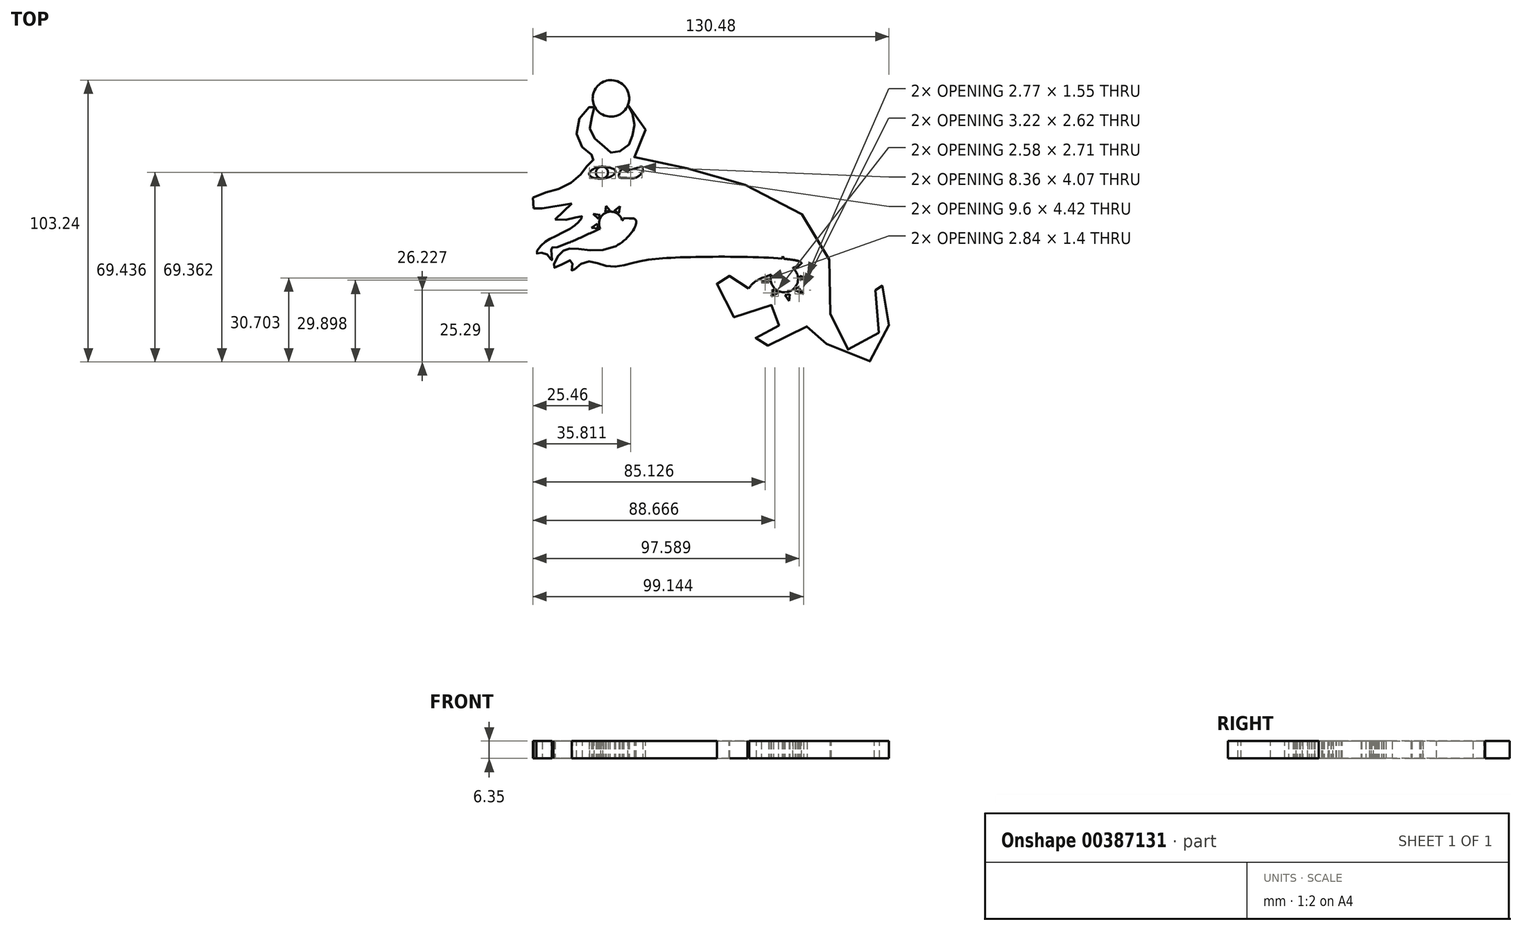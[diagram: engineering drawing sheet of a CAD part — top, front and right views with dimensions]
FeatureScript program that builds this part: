
annotation { "Feature Type Name" : "Feature", "Feature Type Description" : "" }
export const myFeature = defineFeature(function(context is Context, id is Id, definition is map)
    precondition{}
    {
        {
            var Q0;
            Q0=qCreatedBy(makeId("Top.planeOp"),FACE);
            var sketch = newSketch(context, id + "F0", { "sketchPlane" : qUnion([Q0])});
            skLineSegment(sketch, "E0", {"start": v(-40.42, 42.33) * mm, "end": v(-46.54, 36.47) * mm});
            skPoint(sketch, "E1.86.internal.snap0", {"position": v(-47.78, 39.42) * mm});
            skPoint(sketch, "E1.87.internal.snap0", {"position": v(-47.78, 39.42) * mm});
            skPoint(sketch, "E1.88.internal.snap0", {"position": v(-47.78, 39.42) * mm});
            skPoint(sketch, "E1.92.internal.snap0", {"position": v(-47.78, 39.42) * mm});
            skFitSpline(sketch, "E1", {"points": [v(-54.68, 44.52) * mm, v(-45.52, 47.57) * mm, v(-37.48, 52.65) * mm, v(-34.24, 56.77) * mm, v(-32.19, 59.13) * mm, v(-36, 62.36) * mm, v(-38.07, 72.66) * mm, v(-32.48, 78.25) * mm, v(-32.77, 75) * mm, v(-33.49, 68.4) * mm, v(-28.36, 62.95) * mm, v(-25.42, 60.89) * mm, v(-20.12, 63.24) * mm, v(-18.07, 67.95) * mm, v(-17.77, 74.42) * mm, v(-19.83, 78.54) * mm, v(-15.12, 75.6) * mm, v(-13.36, 71.19) * mm, v(-13.95, 66.18) * mm, v(-15.71, 61.48) * mm, v(-17.48, 59.42) * mm, v(-11, 57.07) * mm, v(8.7, 54.12) * mm, v(24, 48.83) * mm, v(41.65, 40) * mm, v(50.77, 30.89) * mm, v(54.6, 16.18) * mm, v(54.3, 2.94) * mm, v(54.88, -3.24) * mm, v(60.18, -10.88) * mm, v(69, -10.59) * mm, v(71.95, -5.3) * mm, v(72.24, 0) * mm, v(70.77, 10.88) * mm, v(70.77, 17.65) * mm, v(72.83, 13.53) * mm, v(74.6, 8.24) * mm, v(75.77, 0) * mm, v(74.3, -10) * mm, v(69.3, -15.3) * mm, v(61.65, -14.41) * mm, v(51.35, -6.77) * mm, v(49.3, 0) * mm, v(44.3, -4.12) * mm, v(37.24, -8.53) * mm, v(27.82, -10.3) * mm, v(24.59, -10.59) * mm, v(27.23, -7.35) * mm, v(24, -5.59) * mm, v(26.94, -4.12) * mm, v(40.47, 0) * mm, v(37.24, 3.82) * mm, v(26.65, 4.12) * mm, v(20.47, 0) * mm, v(16.35, 4.12) * mm, v(13.4, 10) * mm, v(13.11, 13.53) * mm, v(16.94, 11.77) * mm, v(17.23, 16.2) * mm, v(18.4, 11.77) * mm, v(21.35, 9.41) * mm, v(24.3, 11.18) * mm, v(28.41, 14.7) * mm, v(43.7, 20.6) * mm, v(-7.11, 22.3) * mm, v(-18.95, 20.3) * mm, v(-27.77, 19.41) * mm, v(-36, 20.88) * mm, v(-40.42, 17.65) * mm, v(-40.42, 21.47) * mm, v(-46.9, 18.83) * mm, v(-45.13, 23.53) * mm, v(-40.42, 25.89) * mm, v(-24.24, 26.77) * mm, v(-17.48, 36.77) * mm, v(-46.54, 26.18) * mm, v(-47.78, 26.18) * mm, v(-47.78, 22.65) * mm, v(-47.78, 21.47) * mm, v(-50.13, 24.12) * mm, v(-53.36, 24.12) * mm, v(-51.3, 27.36) * mm, v(-47.78, 29.7) * mm, v(-40.42, 33.53) * mm, v(-37.77, 35.89) * mm, v(-36.6, 37.65) * mm, v(-46.54, 36.47) * mm], "startDerivative": vector(701.9, 452.11) * mm, "endDerivative": vector(-908.69, 191.24) * mm});
            skFitSpline(sketch, "E2", {"points": [v(-7.11, 22.3) * mm, v(-2.5, 22.3) * mm, v(0, 22.3) * mm, v(5.3, 22.3) * mm, v(17.23, 18.83) * mm, v(24.3, 11.18) * mm], "startDerivative": vector(37.43, 0.26) * mm, "endDerivative": vector(27.5, -33.03) * mm});
            skFitSpline(sketch, "E3", {"points": [v(-41.53, 27.95) * mm, v(-31.33, 28.53) * mm, v(-24.24, 26.77) * mm], "startDerivative": vector(19.59, 1.14) * mm, "endDerivative": vector(12.47, -4.93) * mm});
            skFitSpline(sketch, "E4", {"points": [v(-34.06, 53.32) * mm, v(-32.1, 55.28) * mm, v(-29.74, 55.87) * mm, v(-26.4, 55.48) * mm, v(-24.44, 54.3) * mm, v(-25.61, 52.53) * mm, v(-28.95, 51.55) * mm, v(-32.88, 51.95) * mm, v(-34.06, 53.32) * mm]});
            skLineSegment(sketch, "E5", {"start": v(-51.3, 40.63) * mm, "end": v(-40.42, 42.33) * mm});
            skLineSegment(sketch, "E6", {"start": v(-54.68, 44.52) * mm, "end": v(-54.4, 40.63) * mm});
            skLineSegment(sketch, "E7", {"start": v(-54.4, 40.63) * mm, "end": v(-51.3, 40.63) * mm});
            skCircle(sketch, "E8", {"center": v(-26.08, 80.9) * mm, "radius": 6.68 * mm});
            skCircle(sketch, "E9", {"center": v(-29.37, 53.7) * mm, "radius": 2.2 * mm});
            skFitSpline(sketch, "E10", {"points": [v(-22.2, 54.9) * mm, v(-20.31, 54.68) * mm, v(-18.2, 54.9) * mm, v(-15, 55.9) * mm, v(-14.77, 55.9) * mm, v(-14.45, 54.77) * mm, v(-15.67, 52.6) * mm, v(-18.15, 51.57) * mm, v(-21.76, 51.8) * mm, v(-23.07, 51.98) * mm, v(-22.2, 54.9) * mm]});
            skCircle(sketch, "E11", {"center": v(-26.15, 35.08) * mm, "radius": 4.3 * mm});
            skLineSegment(sketch, "E12", {"start": v(-24.83, 39.68) * mm, "end": v(-22.74, 41.3) * mm});
            skLineSegment(sketch, "E13", {"start": v(-22.74, 41.3) * mm, "end": v(-23.2, 38.77) * mm});
            skLineSegment(sketch, "E14", {"start": v(-23.2, 38.77) * mm, "end": v(-24.83, 39.68) * mm});
            skLineSegment(sketch, "E15", {"start": v(-21.54, 37.03) * mm, "end": v(-21.13, 35.82) * mm});
            skLineSegment(sketch, "E16", {"start": v(-21.13, 35.82) * mm, "end": v(-19.05, 36.87) * mm});
            skLineSegment(sketch, "E17", {"start": v(-19.05, 36.87) * mm, "end": v(-21.54, 37.03) * mm});
            skLineSegment(sketch, "E18", {"start": v(-21.64, 33.23) * mm, "end": v(-22.15, 32.05) * mm});
            skLineSegment(sketch, "E19", {"start": v(-22.15, 32.05) * mm, "end": v(-19.72, 31.96) * mm});
            skLineSegment(sketch, "E20", {"start": v(-19.72, 31.96) * mm, "end": v(-21.64, 33.23) * mm});
            skLineSegment(sketch, "E21", {"start": v(-25.43, 30.33) * mm, "end": v(-23.93, 30.68) * mm});
            skLineSegment(sketch, "E22", {"start": v(-23.93, 30.68) * mm, "end": v(-24.1, 28.55) * mm});
            skLineSegment(sketch, "E23", {"start": v(-24.1, 28.55) * mm, "end": v(-25.43, 30.33) * mm});
            skLineSegment(sketch, "E24", {"start": v(-29.2, 31.29) * mm, "end": v(-27.38, 30.27) * mm});
            skLineSegment(sketch, "E25", {"start": v(-27.38, 30.27) * mm, "end": v(-29.29, 29) * mm});
            skLineSegment(sketch, "E26", {"start": v(-29.29, 29) * mm, "end": v(-29.2, 31.29) * mm});
            skLineSegment(sketch, "E27", {"start": v(-31.1, 34.97) * mm, "end": v(-30.8, 33.22) * mm});
            skLineSegment(sketch, "E28", {"start": v(-30.8, 33.22) * mm, "end": v(-33.23, 33.45) * mm});
            skLineSegment(sketch, "E29", {"start": v(-33.23, 33.45) * mm, "end": v(-31.1, 34.97) * mm});
            skLineSegment(sketch, "E30", {"start": v(-30.03, 38.11) * mm, "end": v(-30.71, 36.78) * mm});
            skLineSegment(sketch, "E31", {"start": v(-30.71, 36.78) * mm, "end": v(-32.53, 38.6) * mm});
            skLineSegment(sketch, "E32", {"start": v(-32.53, 38.6) * mm, "end": v(-30.03, 38.11) * mm});
            skLineSegment(sketch, "E33", {"start": v(-28.17, 39.29) * mm, "end": v(-26.5, 39.77) * mm});
            skLineSegment(sketch, "E34", {"start": v(-26.5, 39.77) * mm, "end": v(-27.85, 41.48) * mm});
            skLineSegment(sketch, "E35", {"start": v(-27.85, 41.48) * mm, "end": v(-28.17, 39.29) * mm});
            skCircle(sketch, "E36", {"center": v(37.47, 14.81) * mm, "radius": 5.02 * mm});
            skLineSegment(sketch, "E37", {"start": v(40.96, 19.74) * mm, "end": v(42.26, 18.64) * mm});
            skLineSegment(sketch, "E38", {"start": v(42.26, 18.64) * mm, "end": v(43.32, 20.99) * mm});
            skLineSegment(sketch, "E39", {"start": v(43.32, 20.99) * mm, "end": v(40.96, 19.74) * mm});
            skLineSegment(sketch, "E40", {"start": v(43.08, 15.81) * mm, "end": v(43.16, 14.26) * mm});
            skLineSegment(sketch, "E41", {"start": v(43.16, 14.26) * mm, "end": v(45.85, 15.13) * mm});
            skLineSegment(sketch, "E42", {"start": v(45.85, 15.13) * mm, "end": v(43.08, 15.81) * mm});
            skLineSegment(sketch, "E43", {"start": v(42.36, 11.87) * mm, "end": v(41.3, 10.58) * mm});
            skLineSegment(sketch, "E44", {"start": v(41.3, 10.58) * mm, "end": v(44.52, 9.25) * mm});
            skLineSegment(sketch, "E45", {"start": v(44.52, 9.25) * mm, "end": v(42.36, 11.87) * mm});
            skLineSegment(sketch, "E46", {"start": v(39.4, 9.1) * mm, "end": v(37.64, 8.8) * mm});
            skLineSegment(sketch, "E47", {"start": v(37.64, 8.8) * mm, "end": v(39.2, 6.64) * mm});
            skLineSegment(sketch, "E48", {"start": v(39.2, 6.64) * mm, "end": v(39.4, 9.1) * mm});
            skLineSegment(sketch, "E49", {"start": v(35.28, 9.67) * mm, "end": v(33.43, 10.98) * mm});
            skLineSegment(sketch, "E50", {"start": v(33.43, 10.98) * mm, "end": v(32.7, 8.26) * mm});
            skLineSegment(sketch, "E51", {"start": v(32.7, 8.26) * mm, "end": v(35.28, 9.67) * mm});
            skLineSegment(sketch, "E52", {"start": v(31.64, 14.93) * mm, "end": v(31.87, 13.53) * mm});
            skLineSegment(sketch, "E53", {"start": v(31.87, 13.53) * mm, "end": v(29.03, 13.56) * mm});
            skLineSegment(sketch, "E54", {"start": v(29.03, 13.56) * mm, "end": v(31.64, 14.93) * mm});
            skLineSegment(sketch, "E55", {"start": v(33.97, 19.14) * mm, "end": v(32.73, 17.67) * mm});
            skLineSegment(sketch, "E56", {"start": v(32.73, 17.67) * mm, "end": v(31.3, 20.35) * mm});
            skLineSegment(sketch, "E57", {"start": v(31.3, 20.35) * mm, "end": v(33.97, 19.14) * mm});
            skLineSegment(sketch, "E58", {"start": v(36.2, 20.2) * mm, "end": v(37.96, 20.45) * mm});
            skLineSegment(sketch, "E59", {"start": v(37.96, 20.45) * mm, "end": v(36.84, 23) * mm});
            skLineSegment(sketch, "E60", {"start": v(36.84, 23) * mm, "end": v(36.2, 20.2) * mm});
            skSolve(sketch);
        }
        {
            var Q0;
            Q0=makeQuery(id+"F0.imprint","IMPRINT",FACE,{"disambiguationData":[TD([[makeQuery(id+"F0.imprint","IMPRINT",EDGE,{"derivedFrom":sQuery(id+"F0.wireOp",EDGE,"E0")}),1.0]])]});
            var Q1;
            {var subQ0=sQuery(id+"F0.wireOp",EDGE,"E8");var subQ1=sQuery(id+"F0.wireOp",EDGE,"E1");var subQ2=makeQuery(id+"F0.imprint","INTERSECT",VERTEX,{"disambiguationData":[OD(0.0)],"derivedFrom":[subQ1,subQ0]});Q1=makeQuery(id+"F0.imprint","IMPRINT",FACE,{"disambiguationData":[TD([[makeQuery(id+"F0.imprint","IMPRINT",EDGE,{"disambiguationData":[TD([[subQ2,-1.0]])],"derivedFrom":subQ1}),1.0]])]});}
            var Q2;
            {var subQ0=sQuery(id+"F0.wireOp",EDGE,"E9");var subQ1=sQuery(id+"F0.wireOp",EDGE,"E4");var subQ2=makeQuery(id+"F0.imprint","INTERSECT",VERTEX,{"disambiguationData":[OD(0.0)],"derivedFrom":[subQ1,subQ0]});Q2=makeQuery(id+"F0.imprint","IMPRINT",FACE,{"disambiguationData":[TD([[makeQuery(id+"F0.imprint","IMPRINT",EDGE,{"disambiguationData":[TD([[subQ2,1.0]])],"derivedFrom":subQ1}),-1.0]])]});}
            extrude(context, id + "F1", {"entities" : qUnion([Q0, Q1, Q2]), "depth" : 6.35 * mm});
        }
    });
